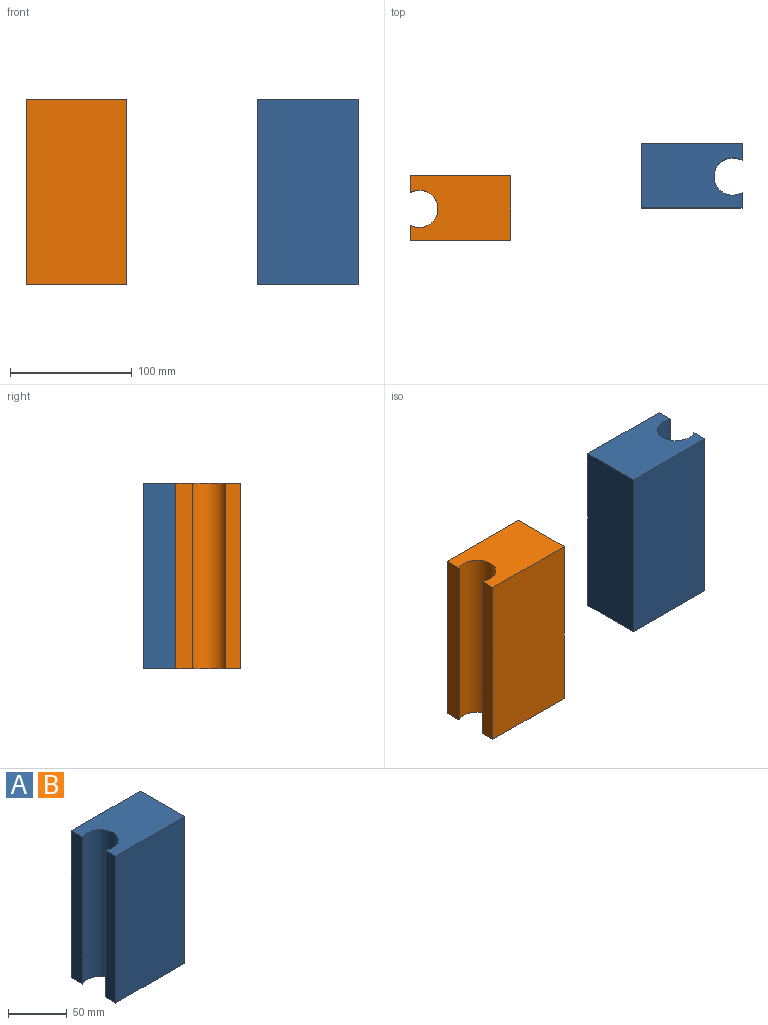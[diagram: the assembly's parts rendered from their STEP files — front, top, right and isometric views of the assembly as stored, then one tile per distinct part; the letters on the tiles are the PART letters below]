
ASSEMBLY  parts=2 mates=1
PART A: 8 faces, bbox 82.6x53x152.4 mm
  f0: plane 152.4x13.77mm, normal (-1,0,0), area 2098.9mm2, adj f4,f5,f6,f7
  f1: plane 152.4x12.53mm, normal (-1,0,0), area 1909.8mm2, adj f2,f4,f6,f7
  f2: plane 152.4x82.58mm, normal (0,-1,0), area 12585.1mm2, adj f1,f3,f6,f7
  f3: plane 152.4x52.99mm, normal (1,0,0), area 8075mm2, adj f2,f5,f6,f7
  f4: cylinder r=15.33mm len=152.4mm, axis (0,0,-1), area 9751.8mm2, adj f0,f1,f6,f7
  f5: plane 152.4x82.58mm, normal (0,1,0), area 12585.1mm2, adj f0,f3,f6,f7
  f6: plane 82.58x52.99mm, normal (0,0,1), area 3784mm2, adj f0,f1,f2,f3,f4,f5
  f7: plane 82.58x52.99mm, normal (0,0,-1), area 3784mm2, adj f0,f1,f2,f3,f4,f5
PART B: same geometry as A
PLACE A rot(axis=(0,1,0),180deg) t=(140.58,-23.53,-1.45)mm
PLACE B t=(-39.28,-50.03,-1.45)mm fixed
MATE slider B.f3 <-> A.f3  axis (1,0,0) through (-2.86,0.03,-1.45)mm
